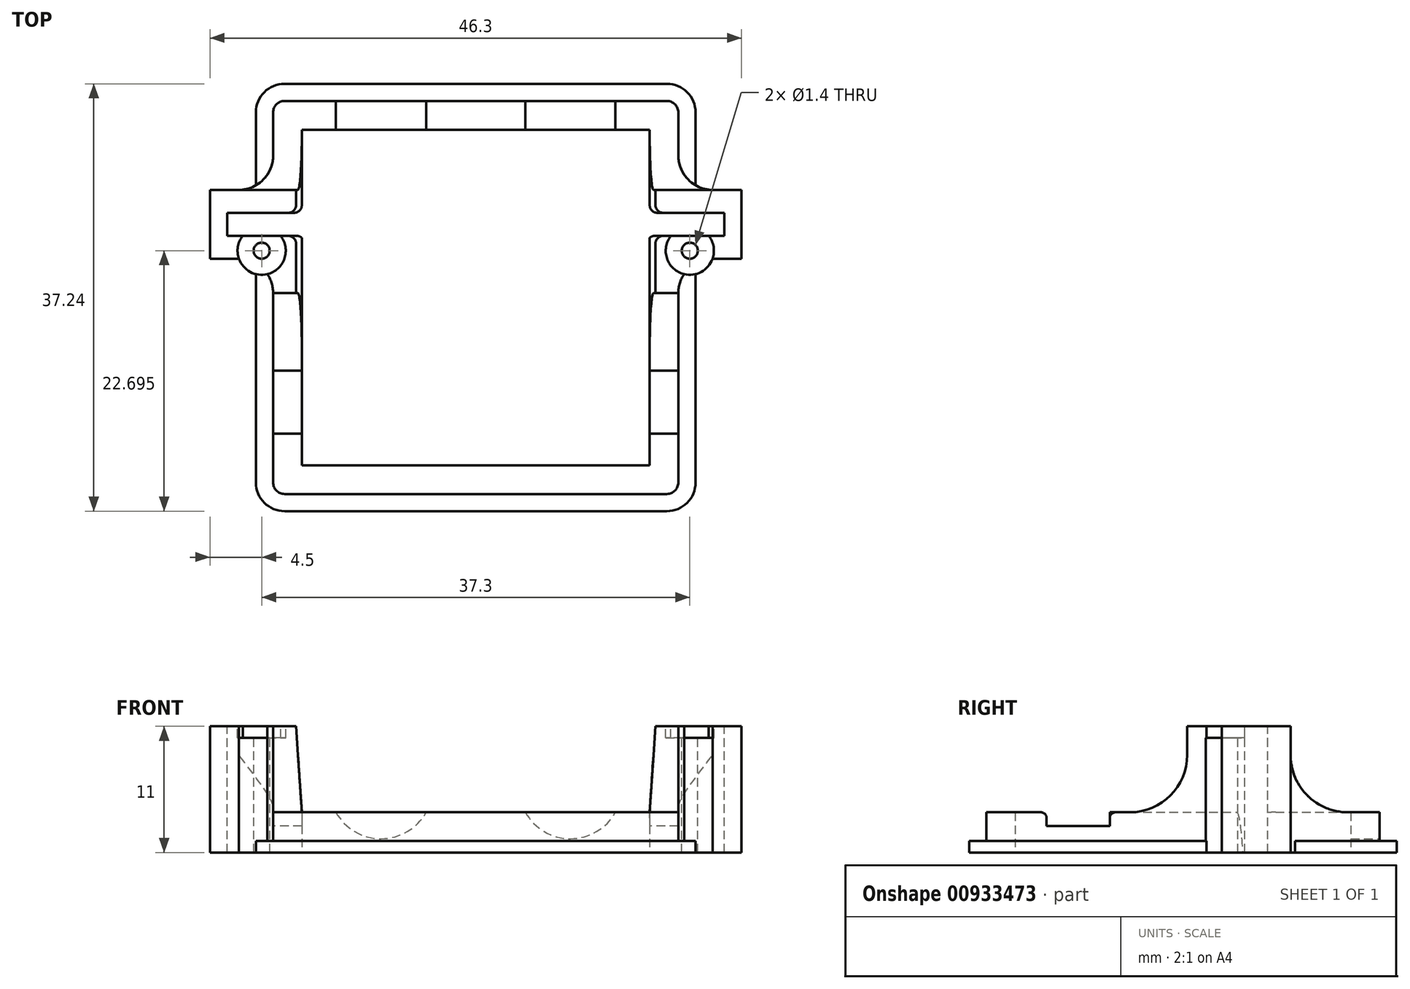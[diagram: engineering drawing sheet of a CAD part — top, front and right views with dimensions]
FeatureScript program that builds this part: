
annotation { "Feature Type Name" : "Feature", "Feature Type Description" : "" }
export const myFeature = defineFeature(function(context is Context, id is Id, definition is map)
    precondition{}
    {
        {
            assignVariable(context, id + "F0", {"name" : "ServoT", "anyValue" : 11});
        }
        {
            assignVariable(context, id + "F1", {"name" : "GlueEdgeH", "anyValue" : 1});
        }
        {
            var Q0;
            Q0=qCreatedBy(makeId("Top.planeOp"),FACE);
            var sketch = newSketch(context, id + "F2", { "sketchPlane" : qUnion([Q0])});
            skLineSegment(sketch, "E0.bottom", {"start": v(15.15, -14.62) * mm, "end": v(-15.15, -14.63) * mm});
            skLineSegment(sketch, "E0.top", {"start": v(15.15, 14.62) * mm, "end": v(-15.15, 14.62) * mm});
            skLineSegment(sketch, "E0.left", {"start": v(15.15, -14.62) * mm, "end": v(15.15, 14.63) * mm});
            skLineSegment(sketch, "E0.right", {"start": v(-15.15, -14.63) * mm, "end": v(-15.15, 14.62) * mm});
            skPoint(sketch, "E0.middle", {"position": v(0, 0) * mm});
            skLineSegment(sketch, "E1.0", {"start": v(16.65, 17.12) * mm, "end": v(-16.65, 17.12) * mm});
            skLineSegment(sketch, "E1.1", {"start": v(17.65, -16.12) * mm, "end": v(17.65, 0.37) * mm});
            skLineSegment(sketch, "E1.2", {"start": v(16.65, -17.12) * mm, "end": v(-16.65, -17.13) * mm});
            skLineSegment(sketch, "E1.3", {"start": v(-17.65, -16.12) * mm, "end": v(-17.65, 0.37) * mm});
            skLineSegment(sketch, "E2", {"start": v(-25.97, 6.37) * mm, "end": v(25.24, 6.37) * mm, "construction": true});
            skLineSegment(sketch, "E3", {"start": v(-23.15, 3.37) * mm, "end": v(-23.15, 9.37) * mm});
            skLineSegment(sketch, "E4", {"start": v(23.15, 3.37) * mm, "end": v(23.15, 9.37) * mm});
            skPoint(sketch, "E5", {"position": v(-23.15, 6.37) * mm});
            skPoint(sketch, "E6", {"position": v(23.15, 6.37) * mm});
            skLineSegment(sketch, "E7", {"start": v(-23.15, 9.37) * mm, "end": v(-20.65, 9.37) * mm});
            skLineSegment(sketch, "E8", {"start": v(-23.15, 3.37) * mm, "end": v(-20.65, 3.37) * mm});
            skLineSegment(sketch, "E9", {"start": v(23.15, 9.37) * mm, "end": v(20.65, 9.37) * mm});
            skLineSegment(sketch, "E10", {"start": v(23.15, 3.37) * mm, "end": v(20.65, 3.37) * mm});
            skLineSegment(sketch, "E11.trimOffspring", {"start": v(-17.65, 12.37) * mm, "end": v(-17.65, 16.12) * mm});
            skLineSegment(sketch, "E12.trimOffspring", {"start": v(17.65, 12.37) * mm, "end": v(17.65, 16.12) * mm});
            skPoint(sketch, "E13.visualSharp", {"position": v(-17.65, 3.37) * mm});
            skArc(sketch, "E13.filletArc", {"start": v(-17.65, 0.37) * mm, "mid": v(-18.53, 2.5) * mm, "end": v(-20.65, 3.37) * mm});
            skPoint(sketch, "E14.visualSharp", {"position": v(-17.65, 9.37) * mm});
            skArc(sketch, "E14.filletArc", {"start": v(-20.65, 9.37) * mm, "mid": v(-18.53, 10.25) * mm, "end": v(-17.65, 12.37) * mm});
            skPoint(sketch, "E15.visualSharp", {"position": v(17.65, 9.37) * mm});
            skArc(sketch, "E15.filletArc", {"start": v(17.65, 12.37) * mm, "mid": v(18.53, 10.25) * mm, "end": v(20.65, 9.37) * mm});
            skPoint(sketch, "E16.visualSharp", {"position": v(17.65, 3.37) * mm});
            skArc(sketch, "E16.filletArc", {"start": v(20.65, 3.37) * mm, "mid": v(18.53, 2.5) * mm, "end": v(17.65, 0.37) * mm});
            skPoint(sketch, "E17.visualSharp", {"position": v(-17.65, 17.12) * mm});
            skArc(sketch, "E17.filletArc", {"start": v(-16.65, 17.12) * mm, "mid": v(-17.36, 16.83) * mm, "end": v(-17.65, 16.12) * mm});
            skPoint(sketch, "E18.visualSharp", {"position": v(17.65, 17.12) * mm});
            skArc(sketch, "E18.filletArc", {"start": v(17.65, 16.12) * mm, "mid": v(17.36, 16.83) * mm, "end": v(16.65, 17.12) * mm});
            skPoint(sketch, "E19.visualSharp", {"position": v(17.65, -17.12) * mm});
            skArc(sketch, "E19.filletArc", {"start": v(16.65, -17.12) * mm, "mid": v(17.36, -16.83) * mm, "end": v(17.65, -16.12) * mm});
            skPoint(sketch, "E20.visualSharp", {"position": v(-17.65, -17.13) * mm});
            skArc(sketch, "E20.filletArc", {"start": v(-17.65, -16.12) * mm, "mid": v(-17.36, -16.83) * mm, "end": v(-16.65, -17.13) * mm});
            skLineSegment(sketch, "E21", {"start": v(0, -21.27) * mm, "end": v(0, 20.45) * mm, "construction": true});
            skPoint(sketch, "E21.endSnap0", {"position": v(0, -17.12) * mm});
            skLineSegment(sketch, "E22", {"start": v(-20.65, -2.75) * mm, "end": v(-20.65, 16.18) * mm, "construction": true});
            skLineSegment(sketch, "E23", {"start": v(20.65, 10.93) * mm, "end": v(20.65, -4.39) * mm, "construction": true});
            skSolve(sketch);
        }
        {
            var Q0;
            Q0 = qSketchRegion(id + "F2", true);
            extrude(context, id + "F3", {"entities" : qUnion([Q0]), "depth" : (getVariable(context, 'ServoT')) * mm, "offsetDistance" : 25 * mm});
        }
        {
            var Q0;
            Q0=makeQuery(id+"F3.opExtrude","SWEPT_FACE",FACE,{"disambiguationData":[OSD([sQuery(id+"F2.wireOp",EDGE,"E1.3")])]});
            var sketch = newSketch(context, id + "F4", { "sketchPlane" : qUnion([Q0])});
            skLineSegment(sketch, "E24.0", {"start": v(17.13, 11) * mm, "end": v(17.13, 3.5) * mm});
            skLineSegment(sketch, "E25.0", {"start": v(16.12, 11) * mm, "end": v(-0.37, 11) * mm});
            skLineSegment(sketch, "E26.0", {"start": v(16.12, 11) * mm, "end": v(17.13, 11) * mm});
            skLineSegment(sketch, "E27.0", {"start": v(-0.37, 11) * mm, "end": v(-0.37, 8.5) * mm});
            skLineSegment(sketch, "E28", {"start": v(17.13, 3.5) * mm, "end": v(4.63, 3.5) * mm});
            skPoint(sketch, "E29.orphan", {"position": v(-0.37, 0) * mm});
            skPoint(sketch, "E30.orphan", {"position": v(17.13, 0) * mm});
            skPoint(sketch, "E31.visualSharp", {"position": v(-0.37, 3.5) * mm});
            skArc(sketch, "E31.filletArc", {"start": v(-0.37, 8.5) * mm, "mid": v(1.09, 4.96) * mm, "end": v(4.63, 3.5) * mm});
            skLineSegment(sketch, "E32.0", {"start": v(-17.12, 11) * mm, "end": v(-17.12, 3.5) * mm});
            skLineSegment(sketch, "E33.0", {"start": v(-17.12, 11) * mm, "end": v(-16.12, 11) * mm});
            skLineSegment(sketch, "E34.0", {"start": v(-12.37, 11) * mm, "end": v(-16.12, 11) * mm});
            skLineSegment(sketch, "E35.0", {"start": v(-9.37, 11) * mm, "end": v(-12.37, 11) * mm});
            skLineSegment(sketch, "E36.0", {"start": v(-9.37, 11) * mm, "end": v(-9.37, 8.5) * mm});
            skLineSegment(sketch, "E37", {"start": v(-17.12, 3.5) * mm, "end": v(-14.37, 3.5) * mm});
            skPoint(sketch, "E38.orphan", {"position": v(-17.12, 0) * mm});
            skPoint(sketch, "E39.visualSharp", {"position": v(-9.37, 3.5) * mm});
            skArc(sketch, "E39.filletArc", {"start": v(-14.37, 3.5) * mm, "mid": v(-10.84, 4.96) * mm, "end": v(-9.37, 8.5) * mm});
            skSolve(sketch);
        }
        {
            var Q0;
            Q0 = qSketchRegion(id + "F4", true);
            extrude(context, id + "F5", {"entities" : qUnion([Q0]), "operationType" : NewBodyOperationType.REMOVE, "endBound" : BoundingType.THROUGH_ALL, "oppositeDirection" : true, "depth" : 25 * mm, "offsetDistance" : 25 * mm, "hasSecondDirection" : true, "secondDirectionBound" : SecondDirectionBoundingType.THROUGH_ALL, "secondDirectionOppositeDirection" : false, "secondDirectionDepth" : 25 * mm});
        }
        {
            var Q0;
            {var subQ0=sQuery(id+"F2.wireOp",EDGE,"E0.right");var subQ1=sQuery(id+"F2.wireOp",EDGE,"E13.filletArc");var subQ2=sQuery(id+"F2.wireOp",EDGE,"E3");Q0=makeQuery(id+"F5.boolean.opBoolean","SPLIT",FACE,{"disambiguationData":[TD([makeQuery(id+"F3.opExtrude","SWEPT_FACE",FACE,{"disambiguationData":[OSD([subQ0])]})])],"derivedFrom":makeQuery(id+"F3.opExtrude","CAP_FACE",FACE,{"disambiguationData":[OSD([sQuery(id+"F2.wireOp",EDGE,"E0.bottom"),sQuery(id+"F2.wireOp",EDGE,"E0.top"),sQuery(id+"F2.wireOp",EDGE,"E0.left"),subQ0,sQuery(id+"F2.wireOp",EDGE,"E1.0"),sQuery(id+"F2.wireOp",EDGE,"E1.1"),sQuery(id+"F2.wireOp",EDGE,"E1.2"),sQuery(id+"F2.wireOp",EDGE,"E1.3"),subQ2,sQuery(id+"F2.wireOp",EDGE,"E4"),sQuery(id+"F2.wireOp",EDGE,"E11.trimOffspring"),sQuery(id+"F2.wireOp",EDGE,"E12.trimOffspring"),subQ1,sQuery(id+"F2.wireOp",EDGE,"E14.filletArc"),sQuery(id+"F2.wireOp",EDGE,"E15.filletArc"),sQuery(id+"F2.wireOp",EDGE,"E16.filletArc"),sQuery(id+"F2.wireOp",EDGE,"E17.filletArc"),sQuery(id+"F2.wireOp",EDGE,"E18.filletArc"),sQuery(id+"F2.wireOp",EDGE,"E19.filletArc"),sQuery(id+"F2.wireOp",EDGE,"E20.filletArc")])],"isStart":false})});}
            var sketch = newSketch(context, id + "F6", { "sketchPlane" : qUnion([Q0])});
            skLineSegment(sketch, "E40.0", {"start": v(-25.97, 6.37) * mm, "end": v(25.24, 6.37) * mm, "construction": true});
            skLineSegment(sketch, "E41.0", {"start": v(-15.15, 5.37) * mm, "end": v(-15.15, 7.37) * mm});
            skLineSegment(sketch, "E42.0", {"start": v(15.15, 5.37) * mm, "end": v(15.15, 7.37) * mm});
            skLineSegment(sketch, "E43", {"start": v(-21.65, 7.37) * mm, "end": v(-15.15, 7.37) * mm});
            skLineSegment(sketch, "E44", {"start": v(-21.65, 5.37) * mm, "end": v(-15.15, 5.37) * mm});
            skLineSegment(sketch, "E45", {"start": v(15.15, 7.38) * mm, "end": v(21.65, 7.38) * mm});
            skLineSegment(sketch, "E46", {"start": v(15.15, 5.38) * mm, "end": v(21.65, 5.38) * mm});
            skPoint(sketch, "E47.orphan", {"position": v(-15.15, 14.62) * mm});
            skPoint(sketch, "E48.orphan", {"position": v(-23.15, 9.37) * mm});
            skPoint(sketch, "E49.orphan", {"position": v(-23.15, 3.37) * mm});
            skPoint(sketch, "E50.orphan", {"position": v(-15.15, -14.63) * mm});
            skPoint(sketch, "E51.orphan", {"position": v(15.15, -14.62) * mm});
            skPoint(sketch, "E52.orphan", {"position": v(15.15, 14.63) * mm});
            skPoint(sketch, "E53.orphan", {"position": v(23.15, 9.37) * mm});
            skPoint(sketch, "E54.orphan", {"position": v(23.15, 3.37) * mm});
            skLineSegment(sketch, "E55", {"start": v(-21.65, 7.37) * mm, "end": v(-21.65, 5.37) * mm});
            skPoint(sketch, "E56", {"position": v(-15.15, 6.37) * mm});
            skPoint(sketch, "E57", {"position": v(15.15, 6.37) * mm});
            skLineSegment(sketch, "E58", {"start": v(21.65, 7.37) * mm, "end": v(21.65, 5.38) * mm});
            skSolve(sketch);
        }
        {
            var Q0;
            Q0 = qSketchRegion(id + "F6", true);
            extrude(context, id + "F7", {"entities" : qUnion([Q0]), "operationType" : NewBodyOperationType.REMOVE, "oppositeDirection" : true, "depth" : (getVariable(context, 'ServoT')) * mm, "offsetDistance" : 25 * mm});
        }
        {
            var Q0;
            {var subQ2=sQuery(id+"F2.wireOp",EDGE,"E0.right");Q0=makeQuery(id+"F7.boolean.opBoolean","SPLIT",EDGE,{"disambiguationData":[TD([makeQuery(id+"F7.opExtrude","SWEPT_FACE",FACE,{"disambiguationData":[OSD([sQuery(id+"F6.wireOp",EDGE,"E44")])]})])],"derivedFrom":makeQuery(id+"F3.opExtrude","CAP_EDGE",EDGE,{"disambiguationData":[OSD([subQ2])],"isStart":false})});}
            var Q1;
            {var subQ0=sQuery(id+"F2.wireOp",EDGE,"E7");var subQ1=sQuery(id+"F2.wireOp",EDGE,"E0.right");Q1=makeQuery(id+"F7.boolean.opBoolean","SPLIT",EDGE,{"disambiguationData":[TD([makeQuery(id+"F3.opExtrude","SWEPT_FACE",FACE,{"disambiguationData":[OSD([subQ0])]})])],"derivedFrom":makeQuery(id+"F3.opExtrude","CAP_EDGE",EDGE,{"disambiguationData":[OSD([subQ1])],"isStart":false})});}
            chamfer(context, id + "F8", {"entities" : qUnion([Q0, Q1]), "chamferType" : ChamferType.TWO_OFFSETS, "width1" : 0.5 * mm, "oppositeDirection" : false, "width2" : 7.5 * mm, "tangentPropagation" : true});
        }
        {
            var Q0;
            {var subQ0=sQuery(id+"F2.wireOp",EDGE,"E9");var subQ1=sQuery(id+"F2.wireOp",EDGE,"E0.left");Q0=makeQuery(id+"F7.boolean.opBoolean","SPLIT",EDGE,{"disambiguationData":[TD([makeQuery(id+"F3.opExtrude","SWEPT_FACE",FACE,{"disambiguationData":[OSD([subQ0])]})])],"derivedFrom":makeQuery(id+"F3.opExtrude","CAP_EDGE",EDGE,{"disambiguationData":[OSD([subQ1])],"isStart":false})});}
            var Q1;
            {var subQ2=sQuery(id+"F2.wireOp",EDGE,"E0.left");Q1=makeQuery(id+"F7.boolean.opBoolean","SPLIT",EDGE,{"disambiguationData":[TD([makeQuery(id+"F7.opExtrude","SWEPT_FACE",FACE,{"disambiguationData":[OSD([sQuery(id+"F6.wireOp",EDGE,"E46")])]})])],"derivedFrom":makeQuery(id+"F3.opExtrude","CAP_EDGE",EDGE,{"disambiguationData":[OSD([subQ2])],"isStart":false})});}
            chamfer(context, id + "F9", {"entities" : qUnion([Q0, Q1]), "chamferType" : ChamferType.TWO_OFFSETS, "width1" : 0.5 * mm, "oppositeDirection" : true, "width2" : 7.5 * mm, "tangentPropagation" : true});
        }
        {
            var Q0;
            {var subQ0=makeQuery(id+"F7.opExtrude","SWEPT_FACE",FACE,{"disambiguationData":[OSD([sQuery(id+"F6.wireOp",EDGE,"E44")])]});var subQ3=sQuery(id+"F2.wireOp",EDGE,"E0.right");Q0=makeQuery(id+"F8.opChamfer","BLEND_EDGE",EDGE,{"blendedFrom":[makeQuery(id+"F7.boolean.opBoolean","SPLIT",EDGE,{"disambiguationData":[TD([subQ0])],"derivedFrom":makeQuery(id+"F3.opExtrude","CAP_EDGE",EDGE,{"disambiguationData":[OSD([subQ3])],"isStart":false})}),makeQuery(id+"F7.boolean.opBoolean","COPY",FACE,{"derivedFrom":subQ0})],"blendedInto":[makeQuery(id+"F7.boolean.opBoolean","COPY",FACE,{"derivedFrom":subQ0})]});}
            var Q1;
            Q1=makeQuery(id+"F7.boolean.opBoolean","COPY",EDGE,{"derivedFrom":makeQuery(id+"F7.opExtrude","SWEPT_EDGE",EDGE,{"disambiguationData":[OSD([sQuery(id+"F2.wireOp",EDGE,"E0.right"),sQuery(id+"F6.wireOp",EDGE,"E41.0"),sQuery(id+"F6.wireOp",EDGE,"E44")])]})});
            var Q2;
            Q2=makeQuery(id+"F7.boolean.opBoolean","COPY",EDGE,{"derivedFrom":makeQuery(id+"F7.opExtrude","SWEPT_EDGE",EDGE,{"disambiguationData":[OSD([sQuery(id+"F2.wireOp",EDGE,"E0.right"),sQuery(id+"F6.wireOp",EDGE,"E41.0"),sQuery(id+"F6.wireOp",EDGE,"E43")])]})});
            var Q3;
            {var subQ0=makeQuery(id+"F7.opExtrude","SWEPT_FACE",FACE,{"disambiguationData":[OSD([sQuery(id+"F6.wireOp",EDGE,"E43")])]});var subQ1=sQuery(id+"F2.wireOp",EDGE,"E7");var subQ2=sQuery(id+"F2.wireOp",EDGE,"E0.right");Q3=makeQuery(id+"F8.opChamfer","BLEND_EDGE",EDGE,{"blendedFrom":[makeQuery(id+"F7.boolean.opBoolean","SPLIT",EDGE,{"disambiguationData":[TD([makeQuery(id+"F3.opExtrude","SWEPT_FACE",FACE,{"disambiguationData":[OSD([subQ1])]})])],"derivedFrom":makeQuery(id+"F3.opExtrude","CAP_EDGE",EDGE,{"disambiguationData":[OSD([subQ2])],"isStart":false})}),makeQuery(id+"F7.boolean.opBoolean","COPY",FACE,{"derivedFrom":subQ0})],"blendedInto":[makeQuery(id+"F7.boolean.opBoolean","COPY",FACE,{"derivedFrom":subQ0})]});}
            var Q4;
            Q4=makeQuery(id+"F7.boolean.opBoolean","COPY",EDGE,{"derivedFrom":makeQuery(id+"F7.opExtrude","SWEPT_EDGE",EDGE,{"disambiguationData":[OSD([sQuery(id+"F6.wireOp",EDGE,"E42.0"),sQuery(id+"F6.wireOp",EDGE,"E45")])]})});
            var Q5;
            {var subQ0=makeQuery(id+"F7.opExtrude","SWEPT_FACE",FACE,{"disambiguationData":[OSD([sQuery(id+"F6.wireOp",EDGE,"E45")])]});var subQ1=sQuery(id+"F2.wireOp",EDGE,"E9");var subQ2=sQuery(id+"F2.wireOp",EDGE,"E0.left");Q5=makeQuery(id+"F9.opChamfer","BLEND_EDGE",EDGE,{"blendedFrom":[makeQuery(id+"F7.boolean.opBoolean","SPLIT",EDGE,{"disambiguationData":[TD([makeQuery(id+"F3.opExtrude","SWEPT_FACE",FACE,{"disambiguationData":[OSD([subQ1])]})])],"derivedFrom":makeQuery(id+"F3.opExtrude","CAP_EDGE",EDGE,{"disambiguationData":[OSD([subQ2])],"isStart":false})}),makeQuery(id+"F7.boolean.opBoolean","COPY",FACE,{"derivedFrom":subQ0})],"blendedInto":[makeQuery(id+"F7.boolean.opBoolean","COPY",FACE,{"derivedFrom":subQ0})]});}
            var Q6;
            {var subQ0=makeQuery(id+"F7.opExtrude","SWEPT_FACE",FACE,{"disambiguationData":[OSD([sQuery(id+"F6.wireOp",EDGE,"E46")])]});var subQ3=sQuery(id+"F2.wireOp",EDGE,"E0.left");Q6=makeQuery(id+"F9.opChamfer","BLEND_EDGE",EDGE,{"blendedFrom":[makeQuery(id+"F7.boolean.opBoolean","SPLIT",EDGE,{"disambiguationData":[TD([subQ0])],"derivedFrom":makeQuery(id+"F3.opExtrude","CAP_EDGE",EDGE,{"disambiguationData":[OSD([subQ3])],"isStart":false})}),makeQuery(id+"F7.boolean.opBoolean","COPY",FACE,{"derivedFrom":subQ0})],"blendedInto":[makeQuery(id+"F7.boolean.opBoolean","COPY",FACE,{"derivedFrom":subQ0})]});}
            var Q7;
            Q7=makeQuery(id+"F7.boolean.opBoolean","COPY",EDGE,{"derivedFrom":makeQuery(id+"F7.opExtrude","SWEPT_EDGE",EDGE,{"disambiguationData":[OSD([sQuery(id+"F6.wireOp",EDGE,"E42.0"),sQuery(id+"F6.wireOp",EDGE,"E46")])]})});
            fillet(context, id + "F10", {"entities" : qUnion([Q0, Q1, Q2, Q3, Q4, Q5, Q6, Q7]), "radius" : 0.7 * mm, "tangentPropagation" : true, "allowEdgeOverflow" : false});
        }
        {
            var Q0;
            Q0=makeQuery(id+"F3.opExtrude","SWEPT_FACE",FACE,{"disambiguationData":[OSD([sQuery(id+"F2.wireOp",EDGE,"E1.0")])]});
            var sketch = newSketch(context, id + "F11", { "sketchPlane" : qUnion([Q0])});
            skLineSegment(sketch, "E59", {"start": v(0, -7.25) * mm, "end": v(0, 20.62) * mm, "construction": true});
            skPoint(sketch, "E59.startSnap0", {"position": v(0, 0) * mm});
            skLineSegment(sketch, "E60", {"start": v(-8.25, 11.18) * mm, "end": v(-8.25, -5.6) * mm, "construction": true});
            skLineSegment(sketch, "E61", {"start": v(8.25, 10.84) * mm, "end": v(8.25, -4.34) * mm, "construction": true});
            skLineSegment(sketch, "E62", {"start": v(-13.01, 1.2) * mm, "end": v(13.24, 1.2) * mm, "construction": true});
            skArc(sketch, "E63", {"start": v(-12.18, 3.5) * mm, "mid": v(-8.25, 1.2) * mm, "end": v(-4.32, 3.5) * mm});
            skArc(sketch, "E64", {"start": v(4.32, 3.5) * mm, "mid": v(8.25, 1.2) * mm, "end": v(12.18, 3.5) * mm});
            skLineSegment(sketch, "E65.0", {"start": v(-12.18, 3.5) * mm, "end": v(-4.32, 3.5) * mm});
            skPoint(sketch, "E66.orphan", {"position": v(16.65, 3.5) * mm});
            skLineSegment(sketch, "E67.trimOffspring", {"start": v(4.32, 3.5) * mm, "end": v(12.18, 3.5) * mm});
            skPoint(sketch, "E68.orphan", {"position": v(-16.65, 3.5) * mm});
            skSolve(sketch);
        }
        {
            var Q0;
            Q0 = qSketchRegion(id + "F11", true);
            extrude(context, id + "F12", {"entities" : qUnion([Q0]), "operationType" : NewBodyOperationType.REMOVE, "endBound" : BoundingType.UP_TO_NEXT, "oppositeDirection" : true, "depth" : 25 * mm, "offsetDistance" : 25 * mm});
        }
        {
            var Q0;
            Q0=makeQuery(id+"F3.opExtrude","SWEPT_FACE",FACE,{"disambiguationData":[OSD([sQuery(id+"F2.wireOp",EDGE,"E1.3")])]});
            var sketch = newSketch(context, id + "F13", { "sketchPlane" : qUnion([Q0])});
            skLineSegment(sketch, "E69.0", {"start": v(14.63, 3.5) * mm, "end": v(14.63, 1.5) * mm, "construction": true});
            skLineSegment(sketch, "E70", {"start": v(9.13, 7.24) * mm, "end": v(9.13, -2.42) * mm, "construction": true});
            skLineSegment(sketch, "E71.bottom", {"start": v(6.38, 3.5) * mm, "end": v(11.88, 3.5) * mm});
            skLineSegment(sketch, "E71.top", {"start": v(6.38, 2.3) * mm, "end": v(11.88, 2.3) * mm});
            skLineSegment(sketch, "E71.left", {"start": v(6.38, 3.5) * mm, "end": v(6.38, 2.3) * mm});
            skLineSegment(sketch, "E71.right", {"start": v(11.88, 3.5) * mm, "end": v(11.88, 2.3) * mm});
            skPoint(sketch, "E72", {"position": v(9.13, 3.5) * mm});
            skSolve(sketch);
        }
        {
            var Q0;
            Q0 = qSketchRegion(id + "F13", true);
            extrude(context, id + "F14", {"entities" : qUnion([Q0]), "operationType" : NewBodyOperationType.REMOVE, "endBound" : BoundingType.THROUGH_ALL, "oppositeDirection" : true, "depth" : 25 * mm, "offsetDistance" : 25 * mm});
        }
        {
            var Q0;
            {var subQ0=sQuery(id+"F4.wireOp",EDGE,"E28");var subQ1=sQuery(id+"F13.wireOp",EDGE,"E71.right");Q0=makeQuery(id+"F14.boolean.opBoolean","COPY",EDGE,{"disambiguationData":[TD([makeQuery(id+"F3.opExtrude","SWEPT_FACE",FACE,{"disambiguationData":[OSD([sQuery(id+"F2.wireOp",EDGE,"E0.left")])]})])],"derivedFrom":makeQuery(id+"F14.opExtrude","SWEPT_EDGE",EDGE,{"disambiguationData":[OSD([sQuery(id+"F2.wireOp",EDGE,"E1.3"),subQ0,sQuery(id+"F13.wireOp",EDGE,"E71.bottom"),subQ1])]})});}
            var Q1;
            {var subQ0=sQuery(id+"F13.wireOp",EDGE,"E71.left");var subQ1=sQuery(id+"F4.wireOp",EDGE,"E28");Q1=makeQuery(id+"F14.boolean.opBoolean","COPY",EDGE,{"disambiguationData":[TD([makeQuery(id+"F3.opExtrude","SWEPT_FACE",FACE,{"disambiguationData":[OSD([sQuery(id+"F2.wireOp",EDGE,"E0.left")])]})])],"derivedFrom":makeQuery(id+"F14.opExtrude","SWEPT_EDGE",EDGE,{"disambiguationData":[OSD([sQuery(id+"F2.wireOp",EDGE,"E1.3"),subQ1,sQuery(id+"F13.wireOp",EDGE,"E71.bottom"),subQ0])]})});}
            var Q2;
            {var subQ0=sQuery(id+"F2.wireOp",EDGE,"E1.3");var subQ1=sQuery(id+"F13.wireOp",EDGE,"E71.left");var subQ2=sQuery(id+"F4.wireOp",EDGE,"E28");Q2=makeQuery(id+"F14.boolean.opBoolean","COPY",EDGE,{"disambiguationData":[TD([makeQuery(id+"F3.opExtrude","SWEPT_FACE",FACE,{"disambiguationData":[OSD([sQuery(id+"F2.wireOp",EDGE,"E0.right")])]})])],"derivedFrom":makeQuery(id+"F14.opExtrude","SWEPT_EDGE",EDGE,{"disambiguationData":[OSD([subQ0,subQ2,sQuery(id+"F13.wireOp",EDGE,"E71.bottom"),subQ1])]})});}
            var Q3;
            {var subQ0=sQuery(id+"F13.wireOp",EDGE,"E71.right");var subQ1=sQuery(id+"F2.wireOp",EDGE,"E1.3");var subQ2=sQuery(id+"F4.wireOp",EDGE,"E28");Q3=makeQuery(id+"F14.boolean.opBoolean","COPY",EDGE,{"disambiguationData":[TD([makeQuery(id+"F3.opExtrude","SWEPT_FACE",FACE,{"disambiguationData":[OSD([sQuery(id+"F2.wireOp",EDGE,"E0.right")])]})])],"derivedFrom":makeQuery(id+"F14.opExtrude","SWEPT_EDGE",EDGE,{"disambiguationData":[OSD([subQ1,subQ2,sQuery(id+"F13.wireOp",EDGE,"E71.bottom"),subQ0])]})});}
            fillet(context, id + "F15", {"entities" : qUnion([Q0, Q1, Q2, Q3]), "radius" : 0.5 * mm, "tangentPropagation" : true, "allowEdgeOverflow" : false});
        }
        {
            var Q0;
            Q0=makeQuery(id+"F3.opExtrude","CAP_FACE",FACE,{"disambiguationData":[OSD([sQuery(id+"F2.wireOp",EDGE,"E0.bottom"),sQuery(id+"F2.wireOp",EDGE,"E0.top"),sQuery(id+"F2.wireOp",EDGE,"E0.left"),sQuery(id+"F2.wireOp",EDGE,"E0.right"),sQuery(id+"F2.wireOp",EDGE,"E1.0"),sQuery(id+"F2.wireOp",EDGE,"E1.1"),sQuery(id+"F2.wireOp",EDGE,"E1.2"),sQuery(id+"F2.wireOp",EDGE,"E1.3"),sQuery(id+"F2.wireOp",EDGE,"E3"),sQuery(id+"F2.wireOp",EDGE,"E4"),sQuery(id+"F2.wireOp",EDGE,"E7"),sQuery(id+"F2.wireOp",EDGE,"E8"),sQuery(id+"F2.wireOp",EDGE,"E9"),sQuery(id+"F2.wireOp",EDGE,"E10"),sQuery(id+"F2.wireOp",EDGE,"E11.trimOffspring"),sQuery(id+"F2.wireOp",EDGE,"E12.trimOffspring"),sQuery(id+"F2.wireOp",EDGE,"E13.filletArc"),sQuery(id+"F2.wireOp",EDGE,"E14.filletArc"),sQuery(id+"F2.wireOp",EDGE,"E15.filletArc"),sQuery(id+"F2.wireOp",EDGE,"E16.filletArc"),sQuery(id+"F2.wireOp",EDGE,"E17.filletArc"),sQuery(id+"F2.wireOp",EDGE,"E18.filletArc"),sQuery(id+"F2.wireOp",EDGE,"E19.filletArc"),sQuery(id+"F2.wireOp",EDGE,"E20.filletArc")])],"isStart":true});
            var sketch = newSketch(context, id + "F16", { "sketchPlane" : qUnion([Q0])});
            skLineSegment(sketch, "E73.0", {"start": v(16.65, 17.12) * mm, "end": v(-16.65, 17.13) * mm});
            skArc(sketch, "E74.0", {"start": v(-17.65, 16.12) * mm, "mid": v(-17.36, 16.83) * mm, "end": v(-16.65, 17.12) * mm});
            skLineSegment(sketch, "E75.0", {"start": v(-17.65, 16.12) * mm, "end": v(-17.65, -3.37) * mm});
            skArc(sketch, "E76.0", {"start": v(16.65, 17.12) * mm, "mid": v(17.36, 16.83) * mm, "end": v(17.65, 16.12) * mm});
            skLineSegment(sketch, "E77.0", {"start": v(17.65, 16.12) * mm, "end": v(17.65, -3.37) * mm});
            skLineSegment(sketch, "E78.0", {"start": v(17.65, -9.37) * mm, "end": v(17.65, -16.12) * mm});
            skArc(sketch, "E79.0", {"start": v(17.65, -16.12) * mm, "mid": v(17.36, -16.83) * mm, "end": v(16.65, -17.12) * mm});
            skLineSegment(sketch, "E80.0", {"start": v(16.65, -17.12) * mm, "end": v(-16.65, -17.12) * mm});
            skArc(sketch, "E81.0", {"start": v(-16.65, -17.12) * mm, "mid": v(-17.36, -16.83) * mm, "end": v(-17.65, -16.12) * mm});
            skLineSegment(sketch, "E82.0", {"start": v(-17.65, -9.37) * mm, "end": v(-17.65, -16.12) * mm});
            skLineSegment(sketch, "E83.0", {"start": v(-19.15, 16.13) * mm, "end": v(-19.15, -3.37) * mm});
            skLineSegment(sketch, "E83.1", {"start": v(19.15, 16.12) * mm, "end": v(19.15, -3.37) * mm});
            skArc(sketch, "E83.2", {"start": v(16.65, 18.62) * mm, "mid": v(18.42, 17.9) * mm, "end": v(19.15, 16.12) * mm});
            skLineSegment(sketch, "E83.3", {"start": v(16.65, 18.62) * mm, "end": v(-16.65, 18.63) * mm});
            skArc(sketch, "E83.4", {"start": v(-19.15, 16.13) * mm, "mid": v(-18.42, 17.9) * mm, "end": v(-16.65, 18.63) * mm});
            skLineSegment(sketch, "E84.0", {"start": v(19.15, -9.37) * mm, "end": v(19.15, -16.12) * mm});
            skLineSegment(sketch, "E84.1", {"start": v(-19.15, -9.37) * mm, "end": v(-19.15, -16.12) * mm});
            skArc(sketch, "E84.2", {"start": v(-16.65, -18.62) * mm, "mid": v(-18.42, -17.9) * mm, "end": v(-19.15, -16.12) * mm});
            skLineSegment(sketch, "E84.3", {"start": v(16.65, -18.62) * mm, "end": v(-16.65, -18.62) * mm});
            skArc(sketch, "E84.4", {"start": v(19.15, -16.12) * mm, "mid": v(18.42, -17.9) * mm, "end": v(16.65, -18.62) * mm});
            skLineSegment(sketch, "E85", {"start": v(-17.65, -3.37) * mm, "end": v(-19.15, -3.37) * mm});
            skLineSegment(sketch, "E86", {"start": v(-17.65, -9.37) * mm, "end": v(-19.15, -9.37) * mm});
            skLineSegment(sketch, "E87", {"start": v(19.15, -9.38) * mm, "end": v(17.65, -9.38) * mm});
            skLineSegment(sketch, "E88", {"start": v(19.15, -3.37) * mm, "end": v(17.65, -3.37) * mm});
            skSolve(sketch);
        }
        {
            var Q0;
            Q0 = qSketchRegion(id + "F16", true);
            extrude(context, id + "F17", {"entities" : qUnion([Q0]), "operationType" : NewBodyOperationType.ADD, "oppositeDirection" : true, "depth" : (getVariable(context, 'GlueEdgeH')) * mm, "offsetDistance" : 25 * mm});
        }
        {
            var Q0;
            {var subQ0=sQuery(id+"F2.wireOp",EDGE,"E8");var subQ1=sQuery(id+"F2.wireOp",EDGE,"E7");var subQ2=sQuery(id+"F2.wireOp",EDGE,"E3");var subQ3=sQuery(id+"F2.wireOp",EDGE,"E0.right");var subQ4=sQuery(id+"F2.wireOp",EDGE,"E13.filletArc");Q0=makeQuery(id+"F5.boolean.opBoolean","SPLIT",FACE,{"disambiguationData":[TD([makeQuery(id+"F3.opExtrude","SWEPT_FACE",FACE,{"disambiguationData":[OSD([subQ3])]})])],"derivedFrom":makeQuery(id+"F3.opExtrude","CAP_FACE",FACE,{"disambiguationData":[OSD([sQuery(id+"F2.wireOp",EDGE,"E0.bottom"),sQuery(id+"F2.wireOp",EDGE,"E0.top"),sQuery(id+"F2.wireOp",EDGE,"E0.left"),subQ3,sQuery(id+"F2.wireOp",EDGE,"E1.0"),sQuery(id+"F2.wireOp",EDGE,"E1.1"),sQuery(id+"F2.wireOp",EDGE,"E1.2"),sQuery(id+"F2.wireOp",EDGE,"E1.3"),subQ2,sQuery(id+"F2.wireOp",EDGE,"E4"),subQ1,subQ0,sQuery(id+"F2.wireOp",EDGE,"E9"),sQuery(id+"F2.wireOp",EDGE,"E10"),sQuery(id+"F2.wireOp",EDGE,"E11.trimOffspring"),sQuery(id+"F2.wireOp",EDGE,"E12.trimOffspring"),subQ4,sQuery(id+"F2.wireOp",EDGE,"E14.filletArc"),sQuery(id+"F2.wireOp",EDGE,"E15.filletArc"),sQuery(id+"F2.wireOp",EDGE,"E16.filletArc"),sQuery(id+"F2.wireOp",EDGE,"E17.filletArc"),sQuery(id+"F2.wireOp",EDGE,"E18.filletArc"),sQuery(id+"F2.wireOp",EDGE,"E19.filletArc"),sQuery(id+"F2.wireOp",EDGE,"E20.filletArc")])],"isStart":false})});}
            var sketch = newSketch(context, id + "F18", { "sketchPlane" : qUnion([Q0])});
            skLineSegment(sketch, "E89.0", {"start": v(-25.97, 6.37) * mm, "end": v(25.24, 6.37) * mm, "construction": true});
            skLineSegment(sketch, "E90", {"start": v(-25.63, 4.07) * mm, "end": v(27.66, 4.08) * mm, "construction": true});
            skLineSegment(sketch, "E91", {"start": v(-18.65, 14.21) * mm, "end": v(-18.65, -2.2) * mm, "construction": true});
            skLineSegment(sketch, "E92", {"start": v(18.65, 13.45) * mm, "end": v(18.65, -2.85) * mm, "construction": true});
            skArc(sketch, "E93", {"start": v(-20.3, 5.37) * mm, "mid": v(-18.65, 1.97) * mm, "end": v(-17, 5.37) * mm});
            skArc(sketch, "E94", {"start": v(17, 5.38) * mm, "mid": v(18.65, 1.98) * mm, "end": v(20.3, 5.38) * mm});
            skLineSegment(sketch, "E95.0", {"start": v(-20.3, 5.37) * mm, "end": v(-17, 5.37) * mm});
            skPoint(sketch, "E96.orphan", {"position": v(-21.65, 5.37) * mm});
            skLineSegment(sketch, "E97.0", {"start": v(17, 5.38) * mm, "end": v(20.3, 5.38) * mm});
            skPoint(sketch, "E98.orphan", {"position": v(21.65, 5.38) * mm});
            skSolve(sketch);
        }
        {
            var Q0;
            Q0 = qSketchRegion(id + "F18", true);
            var Q1;
            Q1=makeQuery(id+"F17.boolean.opBoolean","MERGE",FACE,{"derivedFrom":[makeQuery(id+"F3.opExtrude","CAP_FACE",FACE,{"disambiguationData":[OSD([sQuery(id+"F2.wireOp",EDGE,"E0.bottom"),sQuery(id+"F2.wireOp",EDGE,"E0.top"),sQuery(id+"F2.wireOp",EDGE,"E0.left"),sQuery(id+"F2.wireOp",EDGE,"E0.right"),sQuery(id+"F2.wireOp",EDGE,"E1.0"),sQuery(id+"F2.wireOp",EDGE,"E1.1"),sQuery(id+"F2.wireOp",EDGE,"E1.2"),sQuery(id+"F2.wireOp",EDGE,"E1.3"),sQuery(id+"F2.wireOp",EDGE,"E3"),sQuery(id+"F2.wireOp",EDGE,"E4"),sQuery(id+"F2.wireOp",EDGE,"E7"),sQuery(id+"F2.wireOp",EDGE,"E8"),sQuery(id+"F2.wireOp",EDGE,"E9"),sQuery(id+"F2.wireOp",EDGE,"E10"),sQuery(id+"F2.wireOp",EDGE,"E11.trimOffspring"),sQuery(id+"F2.wireOp",EDGE,"E12.trimOffspring"),sQuery(id+"F2.wireOp",EDGE,"E13.filletArc"),sQuery(id+"F2.wireOp",EDGE,"E14.filletArc"),sQuery(id+"F2.wireOp",EDGE,"E15.filletArc"),sQuery(id+"F2.wireOp",EDGE,"E16.filletArc"),sQuery(id+"F2.wireOp",EDGE,"E17.filletArc"),sQuery(id+"F2.wireOp",EDGE,"E18.filletArc"),sQuery(id+"F2.wireOp",EDGE,"E19.filletArc"),sQuery(id+"F2.wireOp",EDGE,"E20.filletArc")])],"isStart":true}),makeQuery(id+"F17.opExtrude","CAP_FACE",FACE,{"disambiguationData":[OSD([sQuery(id+"F16.wireOp",EDGE,"E73.0"),sQuery(id+"F16.wireOp",EDGE,"E74.0"),sQuery(id+"F16.wireOp",EDGE,"E75.0"),sQuery(id+"F16.wireOp",EDGE,"E76.0"),sQuery(id+"F16.wireOp",EDGE,"E77.0"),sQuery(id+"F16.wireOp",EDGE,"E83.0"),sQuery(id+"F16.wireOp",EDGE,"E83.1"),sQuery(id+"F16.wireOp",EDGE,"E83.2"),sQuery(id+"F16.wireOp",EDGE,"E83.3"),sQuery(id+"F16.wireOp",EDGE,"E83.4"),sQuery(id+"F16.wireOp",EDGE,"E85"),sQuery(id+"F16.wireOp",EDGE,"E88")])],"isStart":true}),makeQuery(id+"F17.opExtrude","CAP_FACE",FACE,{"disambiguationData":[OSD([sQuery(id+"F16.wireOp",EDGE,"E78.0"),sQuery(id+"F16.wireOp",EDGE,"E79.0"),sQuery(id+"F16.wireOp",EDGE,"E80.0"),sQuery(id+"F16.wireOp",EDGE,"E81.0"),sQuery(id+"F16.wireOp",EDGE,"E82.0"),sQuery(id+"F16.wireOp",EDGE,"E84.0"),sQuery(id+"F16.wireOp",EDGE,"E84.1"),sQuery(id+"F16.wireOp",EDGE,"E84.2"),sQuery(id+"F16.wireOp",EDGE,"E84.3"),sQuery(id+"F16.wireOp",EDGE,"E84.4"),sQuery(id+"F16.wireOp",EDGE,"E86"),sQuery(id+"F16.wireOp",EDGE,"E87")])],"isStart":true})]});
            extrude(context, id + "F19", {"entities" : qUnion([Q0]), "operationType" : NewBodyOperationType.ADD, "endBound" : BoundingType.UP_TO_SURFACE, "oppositeDirection" : true, "depth" : 25 * mm, "endBoundEntityFace" : qUnion([Q1]), "offsetDistance" : 25 * mm});
        }
        {
            var Q0;
            {var subQ0=sQuery(id+"F2.wireOp",EDGE,"E8");var subQ1=sQuery(id+"F2.wireOp",EDGE,"E7");var subQ2=sQuery(id+"F2.wireOp",EDGE,"E3");var subQ3=sQuery(id+"F2.wireOp",EDGE,"E0.right");var subQ4=sQuery(id+"F2.wireOp",EDGE,"E13.filletArc");Q0=makeQuery(id+"F19.boolean.opBoolean","MERGE",FACE,{"derivedFrom":[makeQuery(id+"F5.boolean.opBoolean","SPLIT",FACE,{"disambiguationData":[TD([makeQuery(id+"F3.opExtrude","SWEPT_FACE",FACE,{"disambiguationData":[OSD([subQ3])]})])],"derivedFrom":makeQuery(id+"F3.opExtrude","CAP_FACE",FACE,{"disambiguationData":[OSD([sQuery(id+"F2.wireOp",EDGE,"E0.bottom"),sQuery(id+"F2.wireOp",EDGE,"E0.top"),sQuery(id+"F2.wireOp",EDGE,"E0.left"),subQ3,sQuery(id+"F2.wireOp",EDGE,"E1.0"),sQuery(id+"F2.wireOp",EDGE,"E1.1"),sQuery(id+"F2.wireOp",EDGE,"E1.2"),sQuery(id+"F2.wireOp",EDGE,"E1.3"),subQ2,sQuery(id+"F2.wireOp",EDGE,"E4"),subQ1,subQ0,sQuery(id+"F2.wireOp",EDGE,"E9"),sQuery(id+"F2.wireOp",EDGE,"E10"),sQuery(id+"F2.wireOp",EDGE,"E11.trimOffspring"),sQuery(id+"F2.wireOp",EDGE,"E12.trimOffspring"),subQ4,sQuery(id+"F2.wireOp",EDGE,"E14.filletArc"),sQuery(id+"F2.wireOp",EDGE,"E15.filletArc"),sQuery(id+"F2.wireOp",EDGE,"E16.filletArc"),sQuery(id+"F2.wireOp",EDGE,"E17.filletArc"),sQuery(id+"F2.wireOp",EDGE,"E18.filletArc"),sQuery(id+"F2.wireOp",EDGE,"E19.filletArc"),sQuery(id+"F2.wireOp",EDGE,"E20.filletArc")])],"isStart":false})}),makeQuery(id+"F19.opExtrude","CAP_FACE",FACE,{"disambiguationData":[OSD([sQuery(id+"F18.wireOp",EDGE,"E93"),sQuery(id+"F18.wireOp",EDGE,"E95.0")])],"isStart":true})]});}
            var sketch = newSketch(context, id + "F20", { "sketchPlane" : qUnion([Q0])});
            skLineSegment(sketch, "E99.0", {"start": v(-25.63, 4.07) * mm, "end": v(27.66, 4.08) * mm, "construction": true});
            skLineSegment(sketch, "E100.0", {"start": v(-18.65, 14.21) * mm, "end": v(-18.65, -2.2) * mm, "construction": true});
            skCircle(sketch, "E101", {"center": v(-18.65, 4.07) * mm, "radius": 0.7 * mm});
            skPoint(sketch, "E102.0", {"position": v(18.65, 4.08) * mm});
            skCircle(sketch, "E103", {"center": v(18.65, 4.08) * mm, "radius": 0.7 * mm});
            skSolve(sketch);
        }
        {
            var Q0;
            Q0 = qSketchRegion(id + "F20", true);
            extrude(context, id + "F21", {"entities" : qUnion([Q0]), "operationType" : NewBodyOperationType.REMOVE, "endBound" : BoundingType.THROUGH_ALL, "oppositeDirection" : true, "depth" : 25 * mm, "offsetDistance" : 25 * mm});
        }
        {
            var Q0;
            {var subQ0=sQuery(id+"F2.wireOp",EDGE,"E8");var subQ1=sQuery(id+"F2.wireOp",EDGE,"E7");var subQ2=sQuery(id+"F2.wireOp",EDGE,"E3");var subQ3=sQuery(id+"F2.wireOp",EDGE,"E0.right");var subQ4=sQuery(id+"F2.wireOp",EDGE,"E13.filletArc");Q0=makeQuery(id+"F19.boolean.opBoolean","MERGE",FACE,{"derivedFrom":[makeQuery(id+"F5.boolean.opBoolean","SPLIT",FACE,{"disambiguationData":[TD([makeQuery(id+"F3.opExtrude","SWEPT_FACE",FACE,{"disambiguationData":[OSD([subQ3])]})])],"derivedFrom":makeQuery(id+"F3.opExtrude","CAP_FACE",FACE,{"disambiguationData":[OSD([sQuery(id+"F2.wireOp",EDGE,"E0.bottom"),sQuery(id+"F2.wireOp",EDGE,"E0.top"),sQuery(id+"F2.wireOp",EDGE,"E0.left"),subQ3,sQuery(id+"F2.wireOp",EDGE,"E1.0"),sQuery(id+"F2.wireOp",EDGE,"E1.1"),sQuery(id+"F2.wireOp",EDGE,"E1.2"),sQuery(id+"F2.wireOp",EDGE,"E1.3"),subQ2,sQuery(id+"F2.wireOp",EDGE,"E4"),subQ1,subQ0,sQuery(id+"F2.wireOp",EDGE,"E9"),sQuery(id+"F2.wireOp",EDGE,"E10"),sQuery(id+"F2.wireOp",EDGE,"E11.trimOffspring"),sQuery(id+"F2.wireOp",EDGE,"E12.trimOffspring"),subQ4,sQuery(id+"F2.wireOp",EDGE,"E14.filletArc"),sQuery(id+"F2.wireOp",EDGE,"E15.filletArc"),sQuery(id+"F2.wireOp",EDGE,"E16.filletArc"),sQuery(id+"F2.wireOp",EDGE,"E17.filletArc"),sQuery(id+"F2.wireOp",EDGE,"E18.filletArc"),sQuery(id+"F2.wireOp",EDGE,"E19.filletArc"),sQuery(id+"F2.wireOp",EDGE,"E20.filletArc")])],"isStart":false})}),makeQuery(id+"F19.opExtrude","CAP_FACE",FACE,{"disambiguationData":[OSD([sQuery(id+"F18.wireOp",EDGE,"E93"),sQuery(id+"F18.wireOp",EDGE,"E95.0")])],"isStart":true})]});}
            var sketch = newSketch(context, id + "F22", { "sketchPlane" : qUnion([Q0])});
            skCircle(sketch, "E104", {"center": v(-18.65, 4.07) * mm, "radius": 2.1 * mm});
            skCircle(sketch, "E105.0", {"center": v(18.65, 4.08) * mm, "radius": 0.7 * mm, "construction": true});
            skCircle(sketch, "E106", {"center": v(18.65, 4.08) * mm, "radius": 2.1 * mm});
            skSolve(sketch);
        }
        {
            var Q0;
            Q0 = qSketchRegion(id + "F22", true);
            extrude(context, id + "F23", {"entities" : qUnion([Q0]), "operationType" : NewBodyOperationType.REMOVE, "oppositeDirection" : true, "depth" : 1 * mm, "offsetDistance" : 25 * mm});
        }
    });
